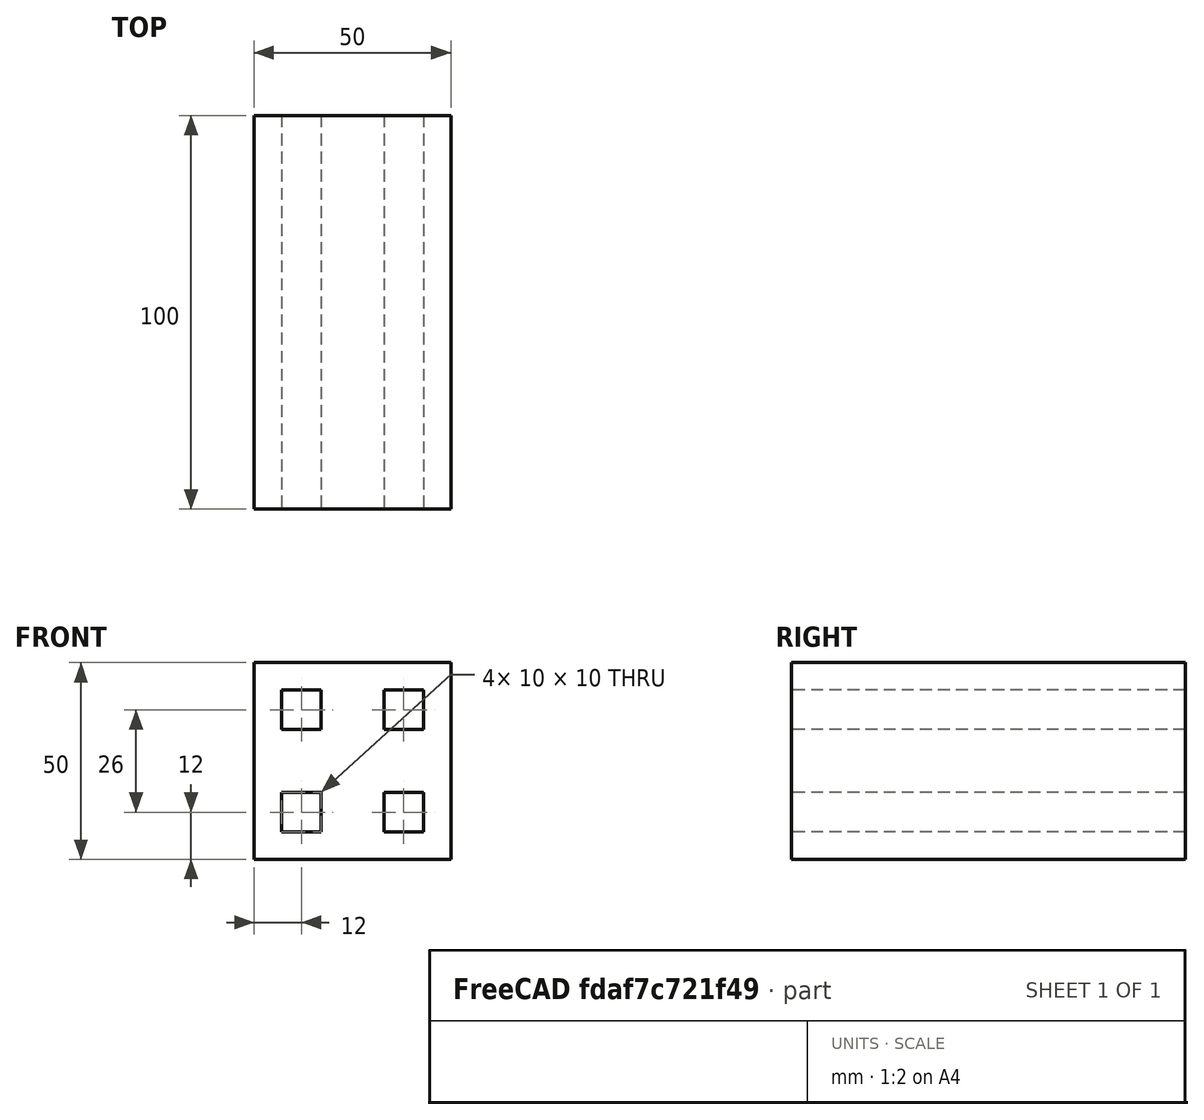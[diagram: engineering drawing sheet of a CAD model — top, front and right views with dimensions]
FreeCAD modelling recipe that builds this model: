
FCSTD DOCUMENT  (FreeCAD 0.16R6707 (Git))
Label: 12-01-ladrillo
License: All rights reserved
LicenseURL: http://en.wikipedia.org/wiki/All_rights_reserved
objects: Sketcher::SketchObject×1, PartDesign::Pad×1
note: 3 computed .brp shape members not serialized (recipe doc carries the construction recipe); baked Part::Feature solids carry a one-line shape summary decoded from their .brp

FEATURE [Sketcher::SketchObject] Sketch002
  Placement = pos=(0,0,0) rot=(-1,0,0;4.71239rad)
  sketch-geometry (20):
    g0: LineSegment StartX=-18 StartY=18 StartZ=0 EndX=-8 EndY=18 EndZ=0
    g1: LineSegment StartX=-8 StartY=18 StartZ=0 EndX=-8 EndY=8 EndZ=0
    g2: LineSegment StartX=-8 StartY=8 StartZ=0 EndX=-18 EndY=8 EndZ=0
    g3: LineSegment StartX=-18 StartY=8 StartZ=0 EndX=-18 EndY=18 EndZ=0
    g4: LineSegment StartX=8 StartY=18 StartZ=0 EndX=18 EndY=18 EndZ=0
    g5: LineSegment StartX=18 StartY=18 StartZ=0 EndX=18 EndY=8 EndZ=0
    g6: LineSegment StartX=18 StartY=8 StartZ=0 EndX=8 EndY=8 EndZ=0
    g7: LineSegment StartX=8 StartY=8 StartZ=0 EndX=8 EndY=18 EndZ=0
    g8: LineSegment StartX=8 StartY=-8 StartZ=0 EndX=18 EndY=-8 EndZ=0
    g9: LineSegment StartX=18 StartY=-8 StartZ=0 EndX=18 EndY=-18 EndZ=0
    g10: LineSegment StartX=18 StartY=-18 StartZ=0 EndX=8 EndY=-18 EndZ=0
    g11: LineSegment StartX=8 StartY=-18 StartZ=0 EndX=8 EndY=-8 EndZ=0
    g12: LineSegment StartX=-18 StartY=-8 StartZ=0 EndX=-8 EndY=-8 EndZ=0
    g13: LineSegment StartX=-8 StartY=-8 StartZ=0 EndX=-8 EndY=-18 EndZ=0
    g14: LineSegment StartX=-8 StartY=-18 StartZ=0 EndX=-18 EndY=-18 EndZ=0
    g15: LineSegment StartX=-18 StartY=-18 StartZ=0 EndX=-18 EndY=-8 EndZ=0
    g16: LineSegment StartX=-25 StartY=25 StartZ=0 EndX=25 EndY=25 EndZ=0
    g17: LineSegment StartX=25 StartY=25 StartZ=0 EndX=25 EndY=-25 EndZ=0
    g18: LineSegment StartX=25 StartY=-25 StartZ=0 EndX=-25 EndY=-25 EndZ=0
    g19: LineSegment StartX=-25 StartY=-25 StartZ=0 EndX=-25 EndY=25 EndZ=0
  constraints (53):
    c: Coincident(g0,g1)
    c: Coincident(g1,g2)
    c: Coincident(g2,g3)
    c: Coincident(g3,g0)
    c: Horizontal(g0)
    c: Horizontal(g2)
    c: Vertical(g1)
    c: Vertical(g3)
    c: DistanceX(g1,g-1) = 8
    c: DistanceY(g-1,g1) = 8
    c: Equal(g0,g1)
    c: DistanceX(g0,g0) = 10
    c: Coincident(g4,g5)
    c: Coincident(g5,g6)
    c: Coincident(g6,g7)
    c: Coincident(g7,g4)
    c: Horizontal(g4)
    c: Horizontal(g6)
    c: Vertical(g5)
    c: Vertical(g7)
    c: Coincident(g8,g9)
    c: Coincident(g9,g10)
    c: Coincident(g10,g11)
    c: Coincident(g11,g8)
    c: Horizontal(g8)
    c: Horizontal(g10)
    c: Vertical(g9)
    c: Vertical(g11)
    c: Coincident(g12,g13)
    c: Coincident(g13,g14)
    c: Coincident(g14,g15)
    c: Coincident(g15,g12)
    c: Horizontal(g12)
    c: Horizontal(g14)
    c: Vertical(g13)
    c: Vertical(g15)
    c: Symmetric(g6,g1,g-2)
    c: Symmetric(g4,g0,g-2)
    c: Symmetric(g2,g12,g-1)
    c: Symmetric(g13,g0,g-1)
    c: Symmetric(g12,g8,g-2)
    c: Symmetric(g9,g14,g-2)
    c: Coincident(g16,g17)
    c: Coincident(g17,g18)
    c: Coincident(g18,g19)
    c: Coincident(g19,g16)
    c: Horizontal(g16)
    c: Horizontal(g18)
    c: Vertical(g17)
    c: Vertical(g19)
    c: Equal(g16,g17)
    c: Symmetric(g16,g17,g-1)
    c: DistanceY(g17,g17) = 50
FEATURE [PartDesign::Pad] Pad
  Length = 100
  Length2 = 100
  Midplane = true
  Placement = pos=(0,0,0) rot=(-1,0,0;4.71239rad)
  Sketch = -> Sketch002
  Type = 0
